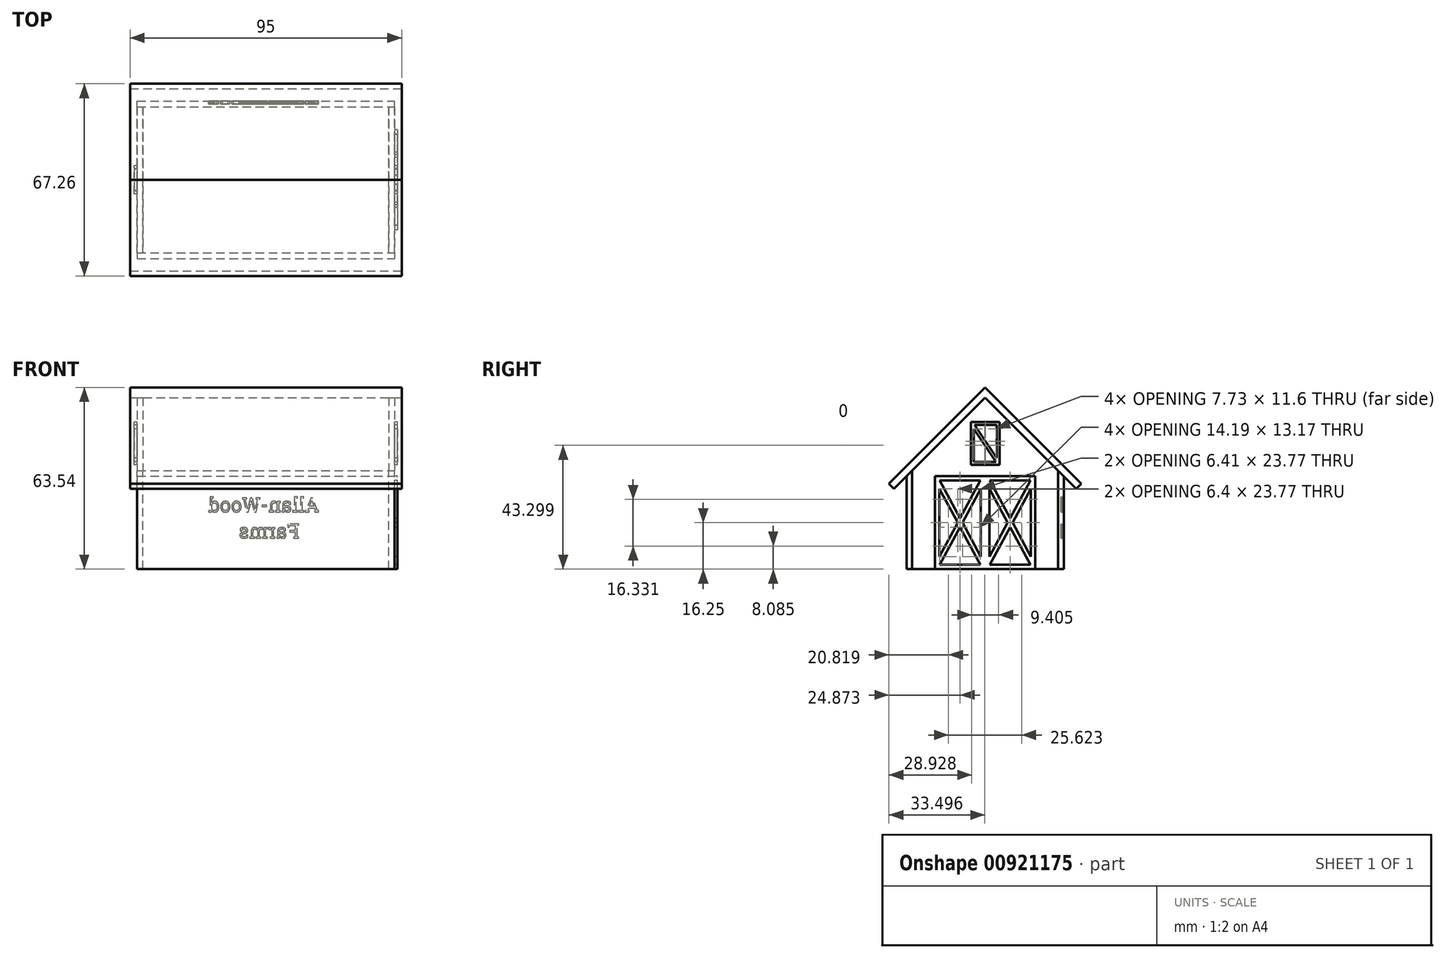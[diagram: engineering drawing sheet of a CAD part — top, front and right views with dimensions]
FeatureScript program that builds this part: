
annotation { "Feature Type Name" : "Feature", "Feature Type Description" : "" }
export const myFeature = defineFeature(function(context is Context, id is Id, definition is map)
    precondition{}
    {
        {
            var Q0;
            Q0=qCreatedBy(makeId("Right.planeOp"),FACE);
            var sketch = newSketch(context, id + "F0", { "sketchPlane" : qUnion([Q0])});
            skLineSegment(sketch, "E0", {"start": v(-27.5, 0) * mm, "end": v(-27.5, 32.5) * mm});
            skLineSegment(sketch, "E1", {"start": v(-27.5, 32.5) * mm, "end": v(0, 60) * mm});
            skLineSegment(sketch, "E2", {"start": v(0, 60) * mm, "end": v(27.5, 32.5) * mm});
            skLineSegment(sketch, "E3", {"start": v(27.5, 32.5) * mm, "end": v(27.5, 0) * mm});
            skLineSegment(sketch, "E4", {"start": v(27.5, 0) * mm, "end": v(-27.5, 0) * mm});
            skLineSegment(sketch, "E5.bottom", {"start": v(-17.51, 0) * mm, "end": v(17.51, 0) * mm});
            skLineSegment(sketch, "E5.top", {"start": v(-17.51, 32.5) * mm, "end": v(17.51, 32.5) * mm});
            skLineSegment(sketch, "E5.left", {"start": v(-17.51, 0) * mm, "end": v(-17.51, 32.5) * mm});
            skLineSegment(sketch, "E5.right", {"start": v(17.51, 0) * mm, "end": v(17.51, 32.5) * mm});
            skLineSegment(sketch, "E6", {"start": v(0, 0) * mm, "end": v(0, 32.5) * mm});
            skLineSegment(sketch, "E7", {"start": v(-17.51, 32.5) * mm, "end": v(0, 0) * mm, "construction": true});
            skLineSegment(sketch, "E8", {"start": v(-17.51, 0) * mm, "end": v(0, 32.5) * mm, "construction": true});
            skLineSegment(sketch, "E9", {"start": v(0, 32.5) * mm, "end": v(17.51, 0) * mm, "construction": true});
            skLineSegment(sketch, "E10", {"start": v(17.51, 32.5) * mm, "end": v(0, 0) * mm, "construction": true});
            skLineSegment(sketch, "E11", {"start": v(-1.5, 4.36) * mm, "end": v(-1.5, 28.14) * mm});
            skLineSegment(sketch, "E12", {"start": v(-1.5, 28.14) * mm, "end": v(-7.9, 16.25) * mm});
            skLineSegment(sketch, "E13", {"start": v(-7.9, 16.25) * mm, "end": v(-1.5, 4.36) * mm});
            skLineSegment(sketch, "E14", {"start": v(-1.66, 31) * mm, "end": v(-15.85, 31) * mm});
            skLineSegment(sketch, "E15", {"start": v(-15.85, 31) * mm, "end": v(-8.76, 17.83) * mm});
            skLineSegment(sketch, "E16", {"start": v(-8.76, 17.83) * mm, "end": v(-1.66, 31) * mm});
            skLineSegment(sketch, "E17", {"start": v(-9.6, 16.25) * mm, "end": v(-16.01, 28.14) * mm});
            skLineSegment(sketch, "E18", {"start": v(-16.01, 28.14) * mm, "end": v(-16.01, 4.36) * mm});
            skLineSegment(sketch, "E19", {"start": v(-16.01, 4.36) * mm, "end": v(-9.6, 16.25) * mm});
            skLineSegment(sketch, "E20", {"start": v(-8.76, 14.67) * mm, "end": v(-15.85, 1.5) * mm});
            skLineSegment(sketch, "E21", {"start": v(-15.85, 1.5) * mm, "end": v(-1.66, 1.5) * mm});
            skLineSegment(sketch, "E22", {"start": v(-1.66, 1.5) * mm, "end": v(-8.76, 14.67) * mm});
            skLineSegment(sketch, "E23.MirrorCS", {"start": v(16.01, 28.14) * mm, "end": v(16.01, 4.36) * mm});
            skLineSegment(sketch, "E24.MirrorCS", {"start": v(9.6, 16.25) * mm, "end": v(16.01, 28.14) * mm});
            skLineSegment(sketch, "E25.MirrorCS", {"start": v(16.01, 4.36) * mm, "end": v(9.6, 16.25) * mm});
            skLineSegment(sketch, "E26.MirrorCS", {"start": v(15.85, 1.5) * mm, "end": v(1.66, 1.5) * mm});
            skLineSegment(sketch, "E27.MirrorCS", {"start": v(8.76, 14.67) * mm, "end": v(15.85, 1.5) * mm});
            skLineSegment(sketch, "E28.MirrorCS", {"start": v(1.66, 1.5) * mm, "end": v(8.76, 14.67) * mm});
            skLineSegment(sketch, "E29.MirrorCS", {"start": v(7.9, 16.25) * mm, "end": v(1.5, 4.36) * mm});
            skLineSegment(sketch, "E30.MirrorCS", {"start": v(1.5, 28.14) * mm, "end": v(7.9, 16.25) * mm});
            skLineSegment(sketch, "E31.MirrorCS", {"start": v(1.5, 4.36) * mm, "end": v(1.5, 28.14) * mm});
            skLineSegment(sketch, "E32.MirrorCS", {"start": v(8.76, 17.83) * mm, "end": v(1.66, 31) * mm});
            skLineSegment(sketch, "E33.MirrorCS", {"start": v(1.66, 31) * mm, "end": v(15.85, 31) * mm});
            skLineSegment(sketch, "E34.MirrorCS", {"start": v(15.85, 31) * mm, "end": v(8.76, 17.83) * mm});
            skLineSegment(sketch, "E35.bottom", {"start": v(-5, 36.5) * mm, "end": v(5, 36.5) * mm});
            skLineSegment(sketch, "E35.top", {"start": v(-5, 51.5) * mm, "end": v(5, 51.5) * mm});
            skLineSegment(sketch, "E35.left", {"start": v(-5, 36.5) * mm, "end": v(-5, 51.5) * mm});
            skLineSegment(sketch, "E35.right", {"start": v(5, 36.5) * mm, "end": v(5, 51.5) * mm});
            skLineSegment(sketch, "E36", {"start": v(-5, 51.5) * mm, "end": v(5, 36.5) * mm, "construction": true});
            skLineSegment(sketch, "E37", {"start": v(-4, 49.1) * mm, "end": v(-4, 37.5) * mm});
            skLineSegment(sketch, "E38", {"start": v(-4, 37.5) * mm, "end": v(3.73, 37.5) * mm});
            skLineSegment(sketch, "E39", {"start": v(3.73, 37.5) * mm, "end": v(-4, 49.1) * mm});
            skLineSegment(sketch, "E40", {"start": v(-3.73, 50.5) * mm, "end": v(4, 50.5) * mm});
            skLineSegment(sketch, "E41", {"start": v(4, 50.5) * mm, "end": v(4, 38.9) * mm});
            skLineSegment(sketch, "E42", {"start": v(4, 38.9) * mm, "end": v(-3.73, 50.5) * mm});
            skLineSegment(sketch, "E43", {"start": v(-33.63, 29.9) * mm, "end": v(0, 63.54) * mm});
            skLineSegment(sketch, "E44", {"start": v(0, 63.54) * mm, "end": v(33.63, 29.9) * mm});
            skLineSegment(sketch, "E45", {"start": v(31.86, 28.14) * mm, "end": v(27.5, 32.5) * mm});
            skLineSegment(sketch, "E46", {"start": v(33.63, 29.9) * mm, "end": v(31.86, 28.14) * mm});
            skLineSegment(sketch, "E47", {"start": v(-33.63, 29.9) * mm, "end": v(-31.86, 28.14) * mm});
            skLineSegment(sketch, "E48", {"start": v(-31.86, 28.14) * mm, "end": v(-27.5, 32.5) * mm});
            skLineSegment(sketch, "E49", {"start": v(-25.5, 0) * mm, "end": v(-25.5, 34.5) * mm});
            skLineSegment(sketch, "E50", {"start": v(25.5, 0) * mm, "end": v(25.5, 34.5) * mm});
            skSolve(sketch);
        }
        {
            var Q0;
            {var subQ0=sQuery(id+"F0.wireOp",EDGE,"E5.left");Q0=makeQuery(id+"F0.imprint","IMPRINT",FACE,{"disambiguationData":[TD([[makeQuery(id+"F0.imprint","IMPRINT",EDGE,{"derivedFrom":subQ0}),-1.0]])]});}
            var Q1;
            {var subQ0=sQuery(id+"F0.wireOp",EDGE,"E5.right");Q1=makeQuery(id+"F0.imprint","IMPRINT",FACE,{"disambiguationData":[TD([[makeQuery(id+"F0.imprint","IMPRINT",EDGE,{"derivedFrom":subQ0}),1.0]])]});}
            var Q2;
            Q2=makeQuery(id+"F0.imprint","IMPRINT",FACE,{"disambiguationData":[TD([[makeQuery(id+"F0.imprint","IMPRINT",EDGE,{"derivedFrom":sQuery(id+"F0.wireOp",EDGE,"E35.bottom")}),1.0]])]});
            extrude(context, id + "F1", {"entities" : qUnion([Q0, Q1, Q2]), "depth" : 1 * mm, "offsetDistance" : 25 * mm});
        }
        {
            var Q0;
            Q0=makeQuery(id+"F0.imprint","IMPRINT",FACE,{"disambiguationData":[TD([[makeQuery(id+"F0.imprint","IMPRINT",EDGE,{"derivedFrom":sQuery(id+"F0.wireOp",EDGE,"E14")}),1.0]])]});
            var Q1;
            Q1=makeQuery(id+"F0.imprint","IMPRINT",FACE,{"disambiguationData":[TD([[makeQuery(id+"F0.imprint","IMPRINT",EDGE,{"derivedFrom":sQuery(id+"F0.wireOp",EDGE,"E11")}),1.0]])]});
            var Q2;
            Q2=makeQuery(id+"F0.imprint","IMPRINT",FACE,{"disambiguationData":[TD([[makeQuery(id+"F0.imprint","IMPRINT",EDGE,{"derivedFrom":sQuery(id+"F0.wireOp",EDGE,"E20")}),1.0]])]});
            var Q3;
            Q3=makeQuery(id+"F0.imprint","IMPRINT",FACE,{"disambiguationData":[TD([[makeQuery(id+"F0.imprint","IMPRINT",EDGE,{"derivedFrom":sQuery(id+"F0.wireOp",EDGE,"E17")}),1.0]])]});
            var Q4;
            Q4=makeQuery(id+"F0.imprint","IMPRINT",FACE,{"disambiguationData":[TD([[makeQuery(id+"F0.imprint","IMPRINT",EDGE,{"derivedFrom":sQuery(id+"F0.wireOp",EDGE,"E32.MirrorCS")}),-1.0]])]});
            var Q5;
            Q5=makeQuery(id+"F0.imprint","IMPRINT",FACE,{"disambiguationData":[TD([[makeQuery(id+"F0.imprint","IMPRINT",EDGE,{"derivedFrom":sQuery(id+"F0.wireOp",EDGE,"E29.MirrorCS")}),-1.0]])]});
            var Q6;
            Q6=makeQuery(id+"F0.imprint","IMPRINT",FACE,{"disambiguationData":[TD([[makeQuery(id+"F0.imprint","IMPRINT",EDGE,{"derivedFrom":sQuery(id+"F0.wireOp",EDGE,"E26.MirrorCS")}),-1.0]])]});
            var Q7;
            Q7=makeQuery(id+"F0.imprint","IMPRINT",FACE,{"disambiguationData":[TD([[makeQuery(id+"F0.imprint","IMPRINT",EDGE,{"derivedFrom":sQuery(id+"F0.wireOp",EDGE,"E23.MirrorCS")}),-1.0]])]});
            var Q8;
            Q8=makeQuery(id+"F0.imprint","IMPRINT",FACE,{"disambiguationData":[TD([[makeQuery(id+"F0.imprint","IMPRINT",EDGE,{"derivedFrom":sQuery(id+"F0.wireOp",EDGE,"E40")}),-1.0]])]});
            var Q9;
            Q9=makeQuery(id+"F0.imprint","IMPRINT",FACE,{"disambiguationData":[TD([[makeQuery(id+"F0.imprint","IMPRINT",EDGE,{"derivedFrom":sQuery(id+"F0.wireOp",EDGE,"E37")}),1.0]])]});
            var Q10;
            Q10=makeQuery(id+"F0.imprint","IMPRINT",FACE,{"disambiguationData":[TD([[makeQuery(id+"F0.imprint","IMPRINT",EDGE,{"derivedFrom":sQuery(id+"F0.wireOp",EDGE,"E35.bottom")}),1.0]])]});
            var Q11;
            {var subQ0=sQuery(id+"F0.wireOp",EDGE,"E5.right");Q11=makeQuery(id+"F0.imprint","IMPRINT",FACE,{"disambiguationData":[TD([[makeQuery(id+"F0.imprint","IMPRINT",EDGE,{"derivedFrom":subQ0}),1.0]])]});}
            var Q12;
            {var subQ0=sQuery(id+"F0.wireOp",EDGE,"E5.left");Q12=makeQuery(id+"F0.imprint","IMPRINT",FACE,{"disambiguationData":[TD([[makeQuery(id+"F0.imprint","IMPRINT",EDGE,{"derivedFrom":subQ0}),-1.0]])]});}
            var Q13;
            {var subQ1=sQuery(id+"F0.wireOp",EDGE,"E5.left");Q13=makeQuery(id+"F0.imprint","IMPRINT",FACE,{"disambiguationData":[TD([[makeQuery(id+"F0.imprint","IMPRINT",EDGE,{"derivedFrom":subQ1}),1.0]])]});}
            extrude(context, id + "F2", {"entities" : qUnion([Q0, Q1, Q2, Q3, Q4, Q5, Q6, Q7, Q8, Q9, Q10, Q11, Q12, Q13]), "oppositeDirection" : true, "depth" : 2 * mm, "offsetDistance" : 25 * mm});
        }
        {
            var Q0;
            {var subQ0=sQuery(id+"F0.wireOp",EDGE,"E0");Q0=makeQuery(id+"F0.imprint","IMPRINT",FACE,{"disambiguationData":[TD([[makeQuery(id+"F0.imprint","IMPRINT",EDGE,{"derivedFrom":subQ0}),-1.0]])]});}
            var Q1;
            {var subQ0=sQuery(id+"F0.wireOp",EDGE,"E3");Q1=makeQuery(id+"F0.imprint","IMPRINT",FACE,{"disambiguationData":[TD([[makeQuery(id+"F0.imprint","IMPRINT",EDGE,{"derivedFrom":subQ0}),-1.0]])]});}
            extrude(context, id + "F3", {"entities" : qUnion([Q0, Q1]), "oppositeDirection" : true, "depth" : 90 * mm, "offsetDistance" : 25 * mm});
        }
        {
            var Q0;
            Q0=makeQuery(id+"F0.imprint","IMPRINT",FACE,{"disambiguationData":[TD([[makeQuery(id+"F0.imprint","IMPRINT",EDGE,{"derivedFrom":sQuery(id+"F0.wireOp",EDGE,"E43")}),-1.0]])]});
            extrude(context, id + "F4", {"entities" : qUnion([Q0]), "oppositeDirection" : true, "depth" : 92.5 * mm, "offsetDistance" : 25 * mm, "hasSecondDirection" : true, "secondDirectionOppositeDirection" : false, "secondDirectionDepth" : 2.5 * mm});
        }
        {
            var Q0;
            Q0=makeQuery(id+"F2.opExtrude","SWEPT_BODY",BODY,{"disambiguationData":[OSD([sQuery(id+"F0.wireOp",EDGE,"E1"),sQuery(id+"F0.wireOp",EDGE,"E2"),sQuery(id+"F0.wireOp",EDGE,"E4"),sQuery(id+"F0.wireOp",EDGE,"E5.bottom"),sQuery(id+"F0.wireOp",EDGE,"E49"),sQuery(id+"F0.wireOp",EDGE,"E50")])]});
            transform(context, id + "F5", {"entities" : qUnion([Q0]), "transformType" : TransformType.TRANSLATION_3D, "dx" : -88 * mm, "dy" : 0 * mm, "dz" : 0 * mm, "makeCopy" : true});
        }
        {
            var Q0;
            Q0=makeQuery(id+"F1.opExtrude","SWEPT_BODY",BODY,{"disambiguationData":[OSD([sQuery(id+"F0.wireOp",EDGE,"E35.bottom"),sQuery(id+"F0.wireOp",EDGE,"E35.top"),sQuery(id+"F0.wireOp",EDGE,"E35.left"),sQuery(id+"F0.wireOp",EDGE,"E35.right"),sQuery(id+"F0.wireOp",EDGE,"E37"),sQuery(id+"F0.wireOp",EDGE,"E38"),sQuery(id+"F0.wireOp",EDGE,"E39"),sQuery(id+"F0.wireOp",EDGE,"E40"),sQuery(id+"F0.wireOp",EDGE,"E41"),sQuery(id+"F0.wireOp",EDGE,"E42")])]});
            transform(context, id + "F6", {"entities" : qUnion([Q0]), "transformType" : TransformType.TRANSLATION_3D, "dx" : -91 * mm, "dy" : 0 * mm, "dz" : 0 * mm, "makeCopy" : true});
        }
        {
            var Q0;
            Q0=makeQuery(id+"F3.opExtrude","SWEPT_FACE",FACE,{"disambiguationData":[OSD([sQuery(id+"F0.wireOp",EDGE,"E3")])]});
            var sketch = newSketch(context, id + "F7", { "sketchPlane" : qUnion([Q0])});
            skText(sketch, "E51", { "text": "Allan-Wood \n    Farms", "fontName": "RobotoSlab-Regular.ttf"});
            const initialGuessF7  = {"E51": [0.0264, 0.02, 1, 0, 0.005]};
            skSetInitialGuess(sketch, initialGuessF7);
            skSolve(sketch);
        }
        {
            var Q0;
            Q0 = qSketchRegion(id + "F7", true);
            extrude(context, id + "F8", {"entities" : qUnion([Q0]), "operationType" : NewBodyOperationType.REMOVE, "oppositeDirection" : true, "depth" : 1 * mm, "offsetDistance" : 25 * mm});
        }
        {
            var Q0;
            Q0 = qSketchRegion(id + "F7", true);
            extrude(context, id + "F9", {"entities" : qUnion([Q0]), "oppositeDirection" : true, "depth" : 1 * mm, "offsetDistance" : 25 * mm});
        }
    });
